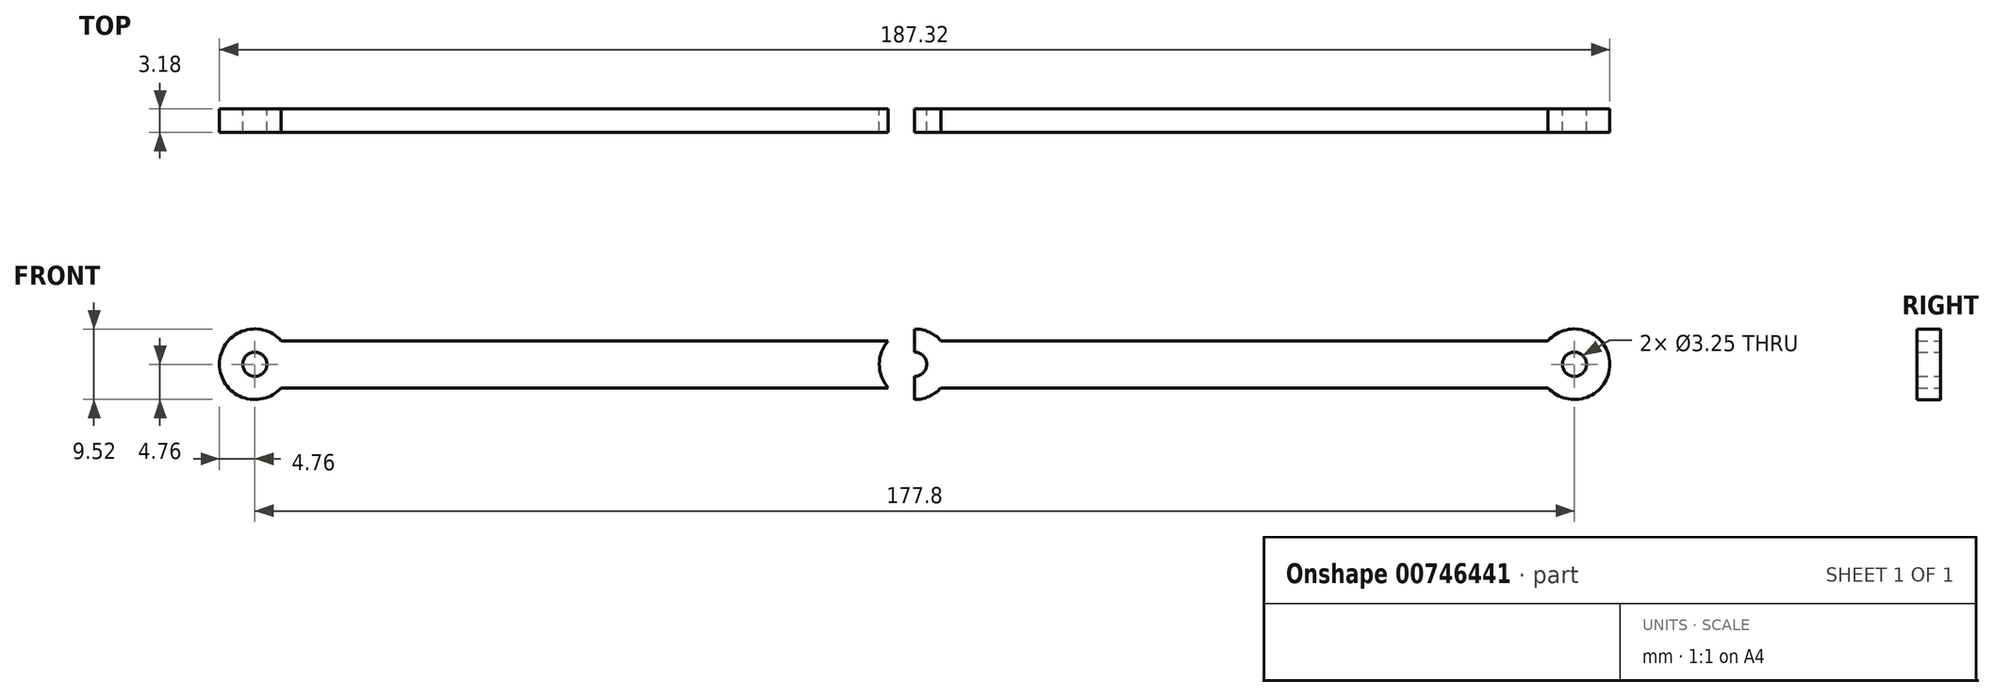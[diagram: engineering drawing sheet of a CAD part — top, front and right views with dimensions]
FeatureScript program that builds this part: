
annotation { "Feature Type Name" : "Feature", "Feature Type Description" : "" }
export const myFeature = defineFeature(function(context is Context, id is Id, definition is map)
    precondition{}
    {
        {
            var Q0;
            Q0=qCreatedBy(makeId("Front.planeOp"),FACE);
            var sketch = newSketch(context, id + "F0", { "sketchPlane" : qUnion([Q0])});
            skLineSegment(sketch, "E0", {"start": v(0, 0) * mm, "end": v(44.45, 0) * mm});
            skCircle(sketch, "E1", {"center": v(44.45, 0) * mm, "radius": 1.63 * mm});
            skArc(sketch, "E2", {"start": v(40.9, -3.17) * mm, "mid": v(49.21, 0) * mm, "end": v(40.9, 3.18) * mm});
            skLineSegment(sketch, "E3.0", {"start": v(0, -3.18) * mm, "end": v(40.9, -3.18) * mm});
            skLineSegment(sketch, "E4.0", {"start": v(0, 3.18) * mm, "end": v(40.9, 3.18) * mm});
            skLineSegment(sketch, "E5", {"start": v(0, 3.18) * mm, "end": v(0, -3.18) * mm});
            skLineSegment(sketch, "E6.MirrorCS", {"start": v(0, 3.18) * mm, "end": v(-40.9, 3.18) * mm});
            skArc(sketch, "E7.MirrorCS", {"start": v(-40.9, -3.17) * mm, "mid": v(-49.21, 0) * mm, "end": v(-40.9, 3.18) * mm});
            skCircle(sketch, "E8.MirrorC", {"center": v(-44.45, 0) * mm, "radius": 1.63 * mm});
            skLineSegment(sketch, "E9.MirrorCS", {"start": v(0, -3.18) * mm, "end": v(-40.9, -3.18) * mm});
            skLineSegment(sketch, "E10", {"start": v(-44.45, 4.76) * mm, "end": v(-44.45, -4.76) * mm});
            skLineSegment(sketch, "E11.MirrorCS", {"start": v(-88.9, 3.18) * mm, "end": v(-48, 3.18) * mm});
            skLineSegment(sketch, "E12.MirrorCS", {"start": v(-88.9, -3.18) * mm, "end": v(-48, -3.18) * mm});
            skLineSegment(sketch, "E13.MirrorCS", {"start": v(-88.9, -3.18) * mm, "end": v(-129.8, -3.18) * mm});
            skLineSegment(sketch, "E14.MirrorCS", {"start": v(-88.9, 3.18) * mm, "end": v(-129.8, 3.18) * mm});
            skArc(sketch, "E15.MirrorCS", {"start": v(-129.8, -3.17) * mm, "mid": v(-138.11, 0) * mm, "end": v(-129.8, 3.18) * mm});
            skCircle(sketch, "E16.MirrorC", {"center": v(-133.35, 0) * mm, "radius": 1.63 * mm});
            skSolve(sketch);
        }
        {
            var Q0;
            {var subQ0=sQuery(id+"F0.wireOp",EDGE,"E6.MirrorCS");Q0=makeQuery(id+"F0.imprint","IMPRINT",FACE,{"disambiguationData":[TD([[makeQuery(id+"F0.imprint","IMPRINT",EDGE,{"derivedFrom":subQ0}),1.0]])]});}
            var Q1;
            Q1=makeQuery(id+"F0.imprint","IMPRINT",FACE,{"disambiguationData":[TD([[makeQuery(id+"F0.imprint","IMPRINT",EDGE,{"derivedFrom":sQuery(id+"F0.wireOp",EDGE,"E1")}),-1.0]])]});
            var Q2;
            {var subQ0=sQuery(id+"F0.wireOp",EDGE,"E11.MirrorCS");Q2=makeQuery(id+"F0.imprint","IMPRINT",FACE,{"disambiguationData":[TD([[makeQuery(id+"F0.imprint","IMPRINT",EDGE,{"derivedFrom":subQ0}),-1.0]])]});}
            var Q3;
            {var subQ0=sQuery(id+"F0.wireOp",EDGE,"E10");var subQ1=sQuery(id+"F0.wireOp",EDGE,"E7.MirrorCS");var subQ8=makeQuery(id+"F0.imprint","INTERSECT",VERTEX,{"disambiguationData":[OD(1.0)],"derivedFrom":[subQ1,subQ0]});Q3=makeQuery(id+"F0.imprint","IMPRINT",FACE,{"disambiguationData":[TD([[makeQuery(id+"F0.imprint","IMPRINT",EDGE,{"disambiguationData":[TD([[subQ8,-1.0]])],"derivedFrom":subQ1}),-1.0]])]});}
            extrude(context, id + "F1", {"entities" : qUnion([Q0, Q1, Q2, Q3]), "depth" : 3.17 * mm, "offsetDistance" : 25.4 * mm});
        }
    });
